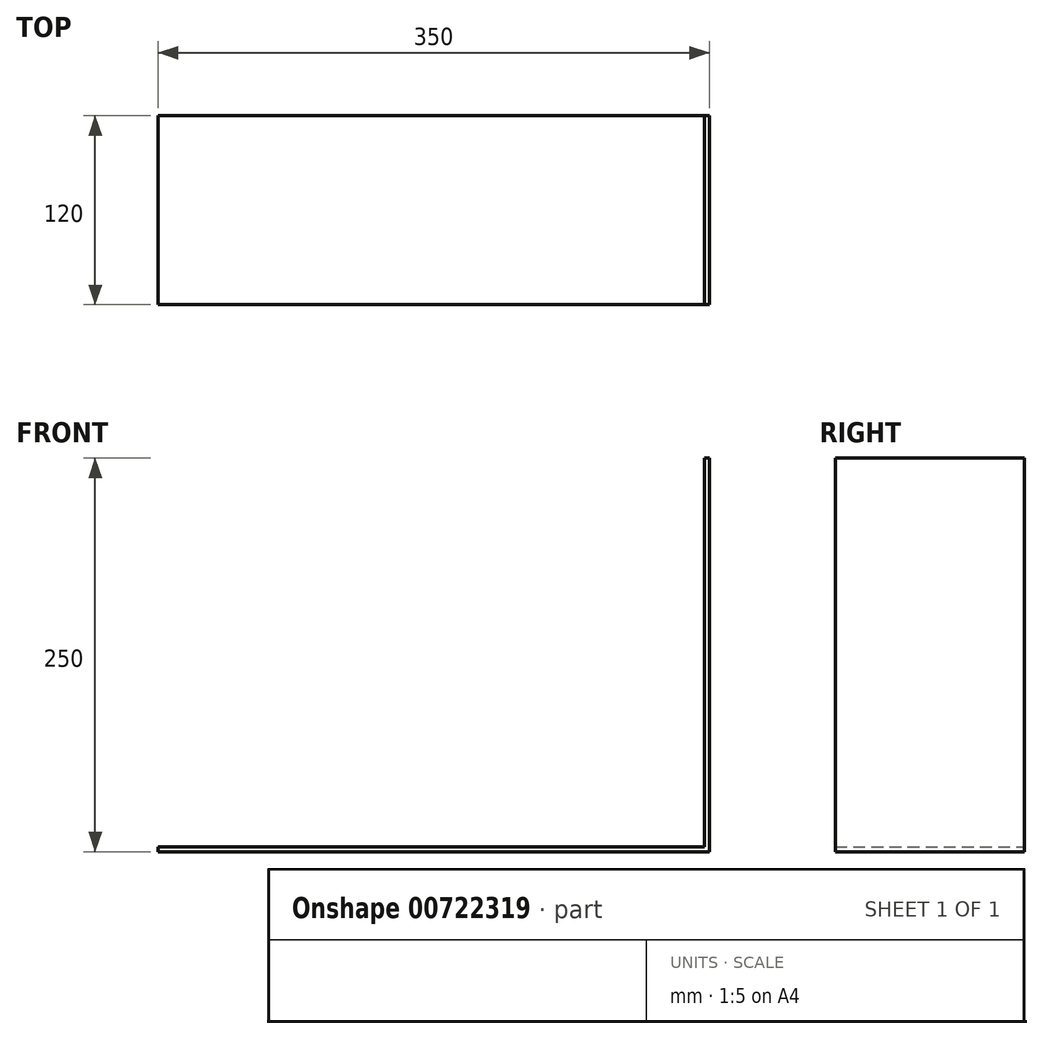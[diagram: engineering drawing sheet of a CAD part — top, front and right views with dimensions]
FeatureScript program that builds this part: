
annotation { "Feature Type Name" : "Feature", "Feature Type Description" : "" }
export const myFeature = defineFeature(function(context is Context, id is Id, definition is map)
    precondition{}
    {
        {
            var Q0;
            Q0=qCreatedBy(makeId("Front.planeOp"),FACE);
            var sketch = newSketch(context, id + "F0", { "sketchPlane" : qUnion([Q0])});
            skLineSegment(sketch, "E0", {"start": v(-350, 0) * mm, "end": v(0, 0) * mm});
            skLineSegment(sketch, "E1", {"start": v(0, 0) * mm, "end": v(0, 250) * mm});
            skLineSegment(sketch, "E2.0", {"start": v(-350, 3) * mm, "end": v(0, 3) * mm});
            skLineSegment(sketch, "E3.0", {"start": v(-3, 0) * mm, "end": v(-3, 250) * mm});
            skLineSegment(sketch, "E4", {"start": v(-350, 3) * mm, "end": v(-350, 0) * mm});
            skLineSegment(sketch, "E5", {"start": v(-3, 250) * mm, "end": v(0, 250) * mm});
            skSolve(sketch);
        }
        {
            var Q0;
            Q0 = qSketchRegion(id + "F0", true);
            extrude(context, id + "F1", {"entities" : qUnion([Q0]), "endBound" : BoundingType.SYMMETRIC, "depth" : 120 * mm, "offsetDistance" : 25 * mm});
        }
    });
